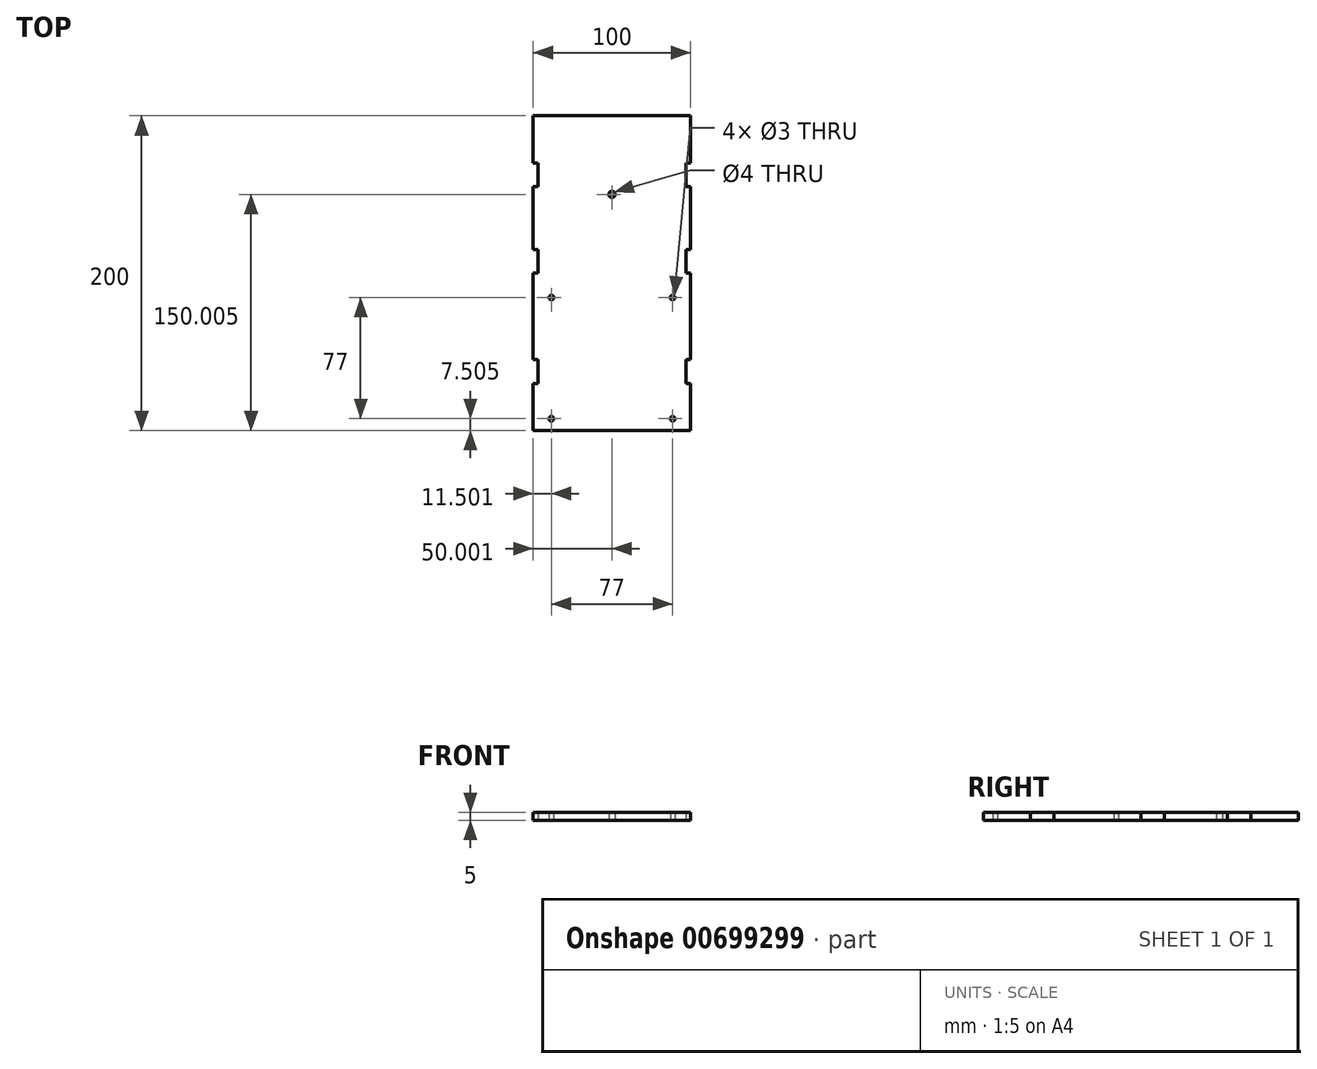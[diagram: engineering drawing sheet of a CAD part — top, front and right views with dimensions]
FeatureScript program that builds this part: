
annotation { "Feature Type Name" : "Feature", "Feature Type Description" : "" }
export const myFeature = defineFeature(function(context is Context, id is Id, definition is map)
    precondition{}
    {
        {
            var Q0;
            Q0=qCreatedBy(makeId("Top.planeOp"),FACE);
            var sketch = newSketch(context, id + "F0", { "sketchPlane" : qUnion([Q0])});
            skLineSegment(sketch, "E0.bottom", {"start": v(-42.37, 133.31) * mm, "end": v(57.63, 133.31) * mm});
            skLineSegment(sketch, "E0.top", {"start": v(-42.37, -66.69) * mm, "end": v(57.63, -66.69) * mm});
            skCircle(sketch, "E1", {"center": v(-30.87, -59.19) * mm, "radius": 1.5 * mm});
            skCircle(sketch, "E2", {"center": v(46.13, -59.19) * mm, "radius": 1.5 * mm});
            skCircle(sketch, "E3", {"center": v(-30.87, 17.81) * mm, "radius": 1.5 * mm});
            skCircle(sketch, "E4", {"center": v(46.13, 17.81) * mm, "radius": 1.5 * mm});
            skPoint(sketch, "E5", {"position": v(7.63, -66.69) * mm});
            skLineSegment(sketch, "E6", {"start": v(7.63, 133.31) * mm, "end": v(7.63, -35.68) * mm, "construction": true});
            skCircle(sketch, "E7", {"center": v(7.63, 83.31) * mm, "radius": 2 * mm});
            skLineSegment(sketch, "E8", {"start": v(57.63, -36.69) * mm, "end": v(54.63, -36.69) * mm});
            skLineSegment(sketch, "E9", {"start": v(54.63, -36.69) * mm, "end": v(54.63, -21.69) * mm});
            skLineSegment(sketch, "E10", {"start": v(54.63, -21.69) * mm, "end": v(57.63, -21.69) * mm});
            skLineSegment(sketch, "E11", {"start": v(57.63, 103.31) * mm, "end": v(54.63, 103.31) * mm});
            skLineSegment(sketch, "E12", {"start": v(54.63, 103.31) * mm, "end": v(54.63, 88.31) * mm});
            skLineSegment(sketch, "E13", {"start": v(54.63, 88.31) * mm, "end": v(57.63, 88.31) * mm});
            skLineSegment(sketch, "E14", {"start": v(57.63, 48.31) * mm, "end": v(54.63, 48.31) * mm});
            skLineSegment(sketch, "E15", {"start": v(54.63, 48.31) * mm, "end": v(54.63, 33.31) * mm});
            skLineSegment(sketch, "E16", {"start": v(54.63, 33.31) * mm, "end": v(57.63, 33.31) * mm});
            skLineSegment(sketch, "E17", {"start": v(57.63, 103.31) * mm, "end": v(57.63, 133.31) * mm});
            skLineSegment(sketch, "E18", {"start": v(57.63, 48.31) * mm, "end": v(57.63, 88.31) * mm});
            skLineSegment(sketch, "E19", {"start": v(57.63, -21.69) * mm, "end": v(57.63, 33.31) * mm});
            skLineSegment(sketch, "E20", {"start": v(57.63, -66.69) * mm, "end": v(57.63, -36.69) * mm});
            skLineSegment(sketch, "E21.MirrorCS", {"start": v(-42.37, 103.31) * mm, "end": v(-42.37, 133.31) * mm});
            skLineSegment(sketch, "E22.MirrorCS", {"start": v(-42.37, -66.69) * mm, "end": v(-42.37, -36.69) * mm});
            skLineSegment(sketch, "E23.MirrorCS", {"start": v(-42.37, 48.31) * mm, "end": v(-39.37, 48.31) * mm});
            skLineSegment(sketch, "E24.MirrorCS", {"start": v(-39.37, 88.31) * mm, "end": v(-42.37, 88.31) * mm});
            skLineSegment(sketch, "E25.MirrorCS", {"start": v(-39.37, 33.31) * mm, "end": v(-42.37, 33.31) * mm});
            skLineSegment(sketch, "E26.MirrorCS", {"start": v(-42.37, 103.31) * mm, "end": v(-39.37, 103.31) * mm});
            skLineSegment(sketch, "E27.MirrorCS", {"start": v(-39.37, -21.69) * mm, "end": v(-42.37, -21.69) * mm});
            skLineSegment(sketch, "E28.MirrorCS", {"start": v(-42.37, -36.69) * mm, "end": v(-39.37, -36.69) * mm});
            skLineSegment(sketch, "E29.MirrorCS", {"start": v(-39.37, -36.69) * mm, "end": v(-39.37, -21.69) * mm});
            skLineSegment(sketch, "E30.MirrorCS", {"start": v(-39.37, 48.31) * mm, "end": v(-39.37, 33.31) * mm});
            skLineSegment(sketch, "E31.MirrorCS", {"start": v(-39.37, 103.31) * mm, "end": v(-39.37, 88.31) * mm});
            skLineSegment(sketch, "E32.MirrorCS", {"start": v(-42.37, -21.69) * mm, "end": v(-42.37, 33.31) * mm});
            skLineSegment(sketch, "E33.MirrorCS", {"start": v(-42.37, 48.31) * mm, "end": v(-42.37, 88.31) * mm});
            skSolve(sketch);
        }
        {
            var Q0;
            Q0 = qSketchRegion(id + "F0", true);
            extrude(context, id + "F1", {"entities" : qUnion([Q0]), "depth" : 5 * mm, "offsetDistance" : 25 * mm});
        }
    });
